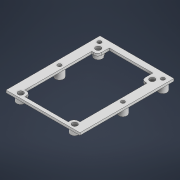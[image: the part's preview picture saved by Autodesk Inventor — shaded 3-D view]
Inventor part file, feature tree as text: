
AUTODESK INVENTOR PART (.ipt)
format: ipt  version: 2021 (Build 250183000, 183)  size: 223,744 bytes
history: native  units: mm
features: extrude x5, sketch x5, fillet x1
ambient origin geometry x8: Origin, YZ Plane, XZ Plane, XY Plane, X Axis, Y Axis, Z Axis, Center Point
bodies: Volumenkörper1 (feature_tree)
feature tree (11):
  extrude  "Extrusion1"  Depth=80.0mm
  sketch  "Skizze3"  dims[d4=27.0mm d5=27.0mm]
  extrude  "Extrusion2"  Depth=3.2mm
  extrude  "Extrusion3"  Depth=27.0mm
  extrude  "Extrusion4"  Depth=5.0mm
  extrude  "Extrusion5"  Depth=3.5mm
  fillet  "Rundung1"  Radius=27.0mm
  sketch  "Skizze1"  dims[d0=63.0mm d1=80.0mm]
  sketch  "Skizze2"  dims[d2=3.2mm d3=3.2mm]
  sketch  "Skizze4"  dims[d6=5.0mm d7=5.0mm]
  sketch  "Skizze5"  dims[d8=3.2mm d9=3.2mm d10=27.0mm d11=27.0mm d12=34.0mm d13=34.0mm d14=2.0mm d15=0.0mm d16=7.0mm d17=7.0mm d18=7.0mm d19=7.0mm d20=6.5mm d21=0.0mm d22=7.0mm d23=7.0mm d24=7.0mm d25=7.0mm d26=23.0mm d27=23.0mm d28=23.0mm d29=23.0mm d31=10.0mm d32=10.0mm d33=66.0mm d34=66.0mm d35=6.0mm d36=0.0mm d37=4.5mm d38=4.5mm d39=4.5mm d40=4.5mm d41=6.0mm d42=0.0mm d43=15.0mm d44=8.0mm d45=8.0mm d46=8.0mm d47=6.0mm d48=0.0mm d49=3.0mm d50=13.0mm d51=13.0mm d52=13.0mm d53=13.0mm d54=5.0mm d55=8.0mm d56=8.0mm d57=15.0mm d58=15.0mm d59=3.5mm]
